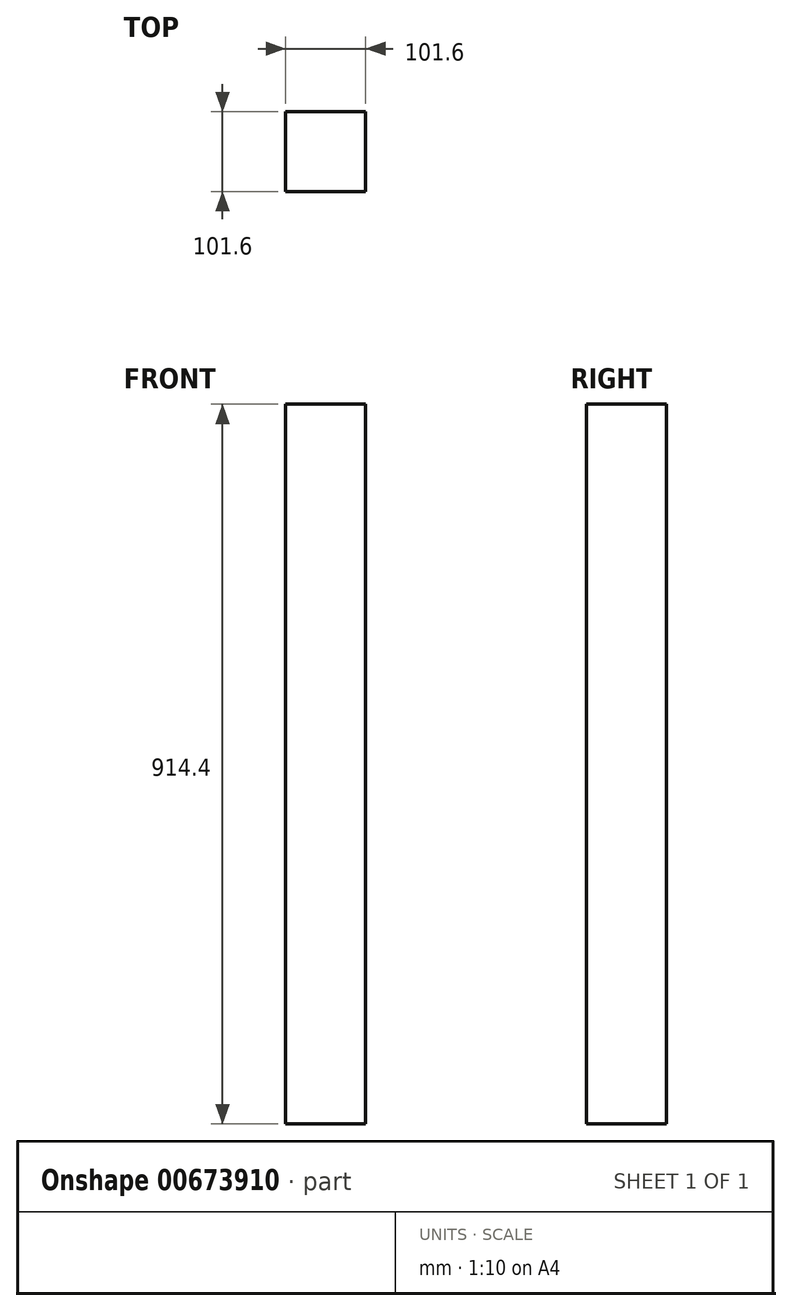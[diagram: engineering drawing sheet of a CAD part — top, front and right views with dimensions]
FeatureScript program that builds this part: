
annotation { "Feature Type Name" : "Feature", "Feature Type Description" : "" }
export const myFeature = defineFeature(function(context is Context, id is Id, definition is map)
    precondition{}
    {
        {
            var Q0;
            Q0=qCreatedBy(makeId("Top.planeOp"),FACE);
            var sketch = newSketch(context, id + "F0", { "sketchPlane" : qUnion([Q0])});
            skLineSegment(sketch, "E0.bottom", {"start": v(50.8, 50.8) * mm, "end": v(-50.8, 50.8) * mm});
            skLineSegment(sketch, "E0.top", {"start": v(50.8, -50.8) * mm, "end": v(-50.8, -50.8) * mm});
            skLineSegment(sketch, "E0.left", {"start": v(50.8, 50.8) * mm, "end": v(50.8, -50.8) * mm});
            skLineSegment(sketch, "E0.right", {"start": v(-50.8, 50.8) * mm, "end": v(-50.8, -50.8) * mm});
            skPoint(sketch, "E0.middle", {"position": v(0, 0) * mm});
            skSolve(sketch);
        }
        {
            var Q0;
            Q0 = qSketchRegion(id + "F0", true);
            extrude(context, id + "F1", {"entities" : qUnion([Q0]), "depth" : 914.4 * mm, "offsetDistance" : 25.4 * mm});
        }
    });
